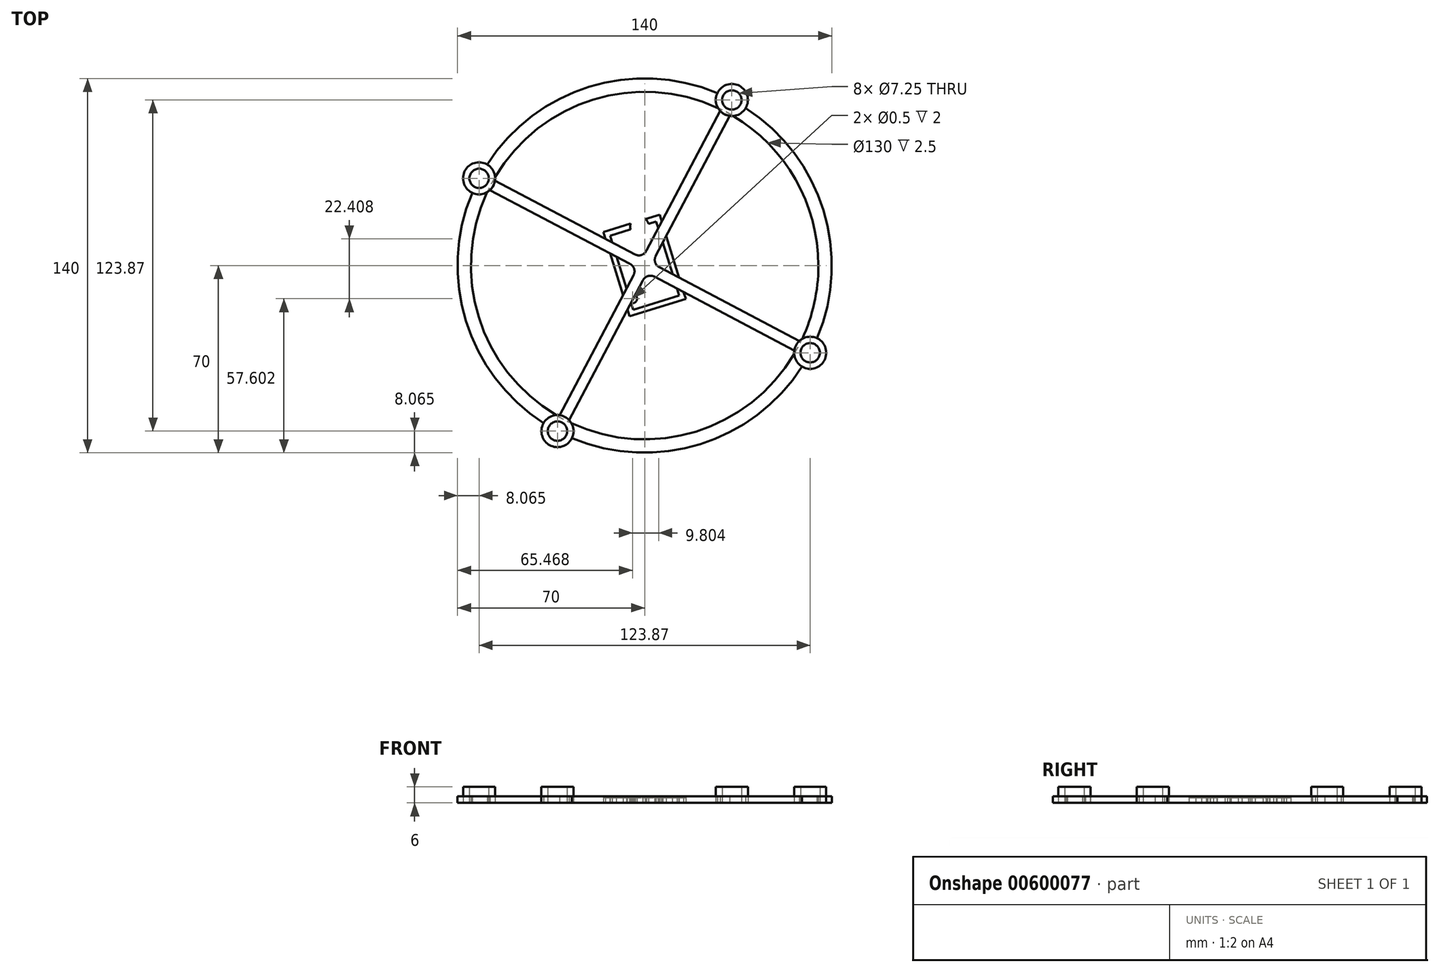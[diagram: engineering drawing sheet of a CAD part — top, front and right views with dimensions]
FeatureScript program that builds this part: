
annotation { "Feature Type Name" : "Feature", "Feature Type Description" : "" }
export const myFeature = defineFeature(function(context is Context, id is Id, definition is map)
    precondition{}
    {
        {
            var Q0;
            Q0=qCreatedBy(makeId("Top.planeOp"),FACE);
            var sketch = newSketch(context, id + "F0", { "sketchPlane" : qUnion([Q0])});
            skCircle(sketch, "E0", {"center": v(-61.93, 32.62) * mm, "radius": 3.62 * mm});
            skCircle(sketch, "E1", {"center": v(-61.93, 32.62) * mm, "radius": 6 * mm});
            skCircle(sketch, "E2", {"center": v(0, 0) * mm, "radius": 70 * mm});
            skCircle(sketch, "E3", {"center": v(0, 0) * mm, "radius": 65 * mm});
            skCircle(sketch, "E4.1.0", {"center": v(-32.62, -61.93) * mm, "radius": 3.62 * mm});
            skCircle(sketch, "E4.1.1", {"center": v(-32.62, -61.93) * mm, "radius": 6 * mm});
            skCircle(sketch, "E4.2.0", {"center": v(61.93, -32.62) * mm, "radius": 3.62 * mm});
            skCircle(sketch, "E4.2.1", {"center": v(61.93, -32.62) * mm, "radius": 6 * mm});
            skCircle(sketch, "E4.3.0", {"center": v(32.62, 61.93) * mm, "radius": 3.62 * mm});
            skCircle(sketch, "E4.3.1", {"center": v(32.62, 61.93) * mm, "radius": 6 * mm});
            skLineSegment(sketch, "E5", {"start": v(32.62, 61.93) * mm, "end": v(-32.62, -61.93) * mm});
            skLineSegment(sketch, "E6", {"start": v(-56.55, 32.05) * mm, "end": v(-3.59, 4.15) * mm});
            skArc(sketch, "E7", {"start": v(-3.59, 4.15) * mm, "mid": v(-1.1, 3.97) * mm, "end": v(0.72, 5.66) * mm});
            skLineSegment(sketch, "E8", {"start": v(0.72, 5.66) * mm, "end": v(28.5, 58.42) * mm});
            skLineSegment(sketch, "E9", {"start": v(61.93, -32.62) * mm, "end": v(-61.93, 32.62) * mm});
            skLineSegment(sketch, "E10.1.0", {"start": v(-5.66, 0.72) * mm, "end": v(-58.42, 28.5) * mm});
            skArc(sketch, "E10.1.1", {"start": v(-4.15, -3.59) * mm, "mid": v(-3.97, -1.1) * mm, "end": v(-5.66, 0.72) * mm});
            skLineSegment(sketch, "E10.1.2", {"start": v(-32.05, -56.55) * mm, "end": v(-4.15, -3.59) * mm});
            skLineSegment(sketch, "E10.2.0", {"start": v(-0.72, -5.66) * mm, "end": v(-28.5, -58.42) * mm});
            skArc(sketch, "E10.2.1", {"start": v(3.59, -4.15) * mm, "mid": v(1.1, -3.97) * mm, "end": v(-0.72, -5.66) * mm});
            skLineSegment(sketch, "E10.2.2", {"start": v(56.55, -32.05) * mm, "end": v(3.59, -4.15) * mm});
            skLineSegment(sketch, "E10.3.0", {"start": v(5.66, -0.72) * mm, "end": v(58.42, -28.5) * mm});
            skArc(sketch, "E10.3.1", {"start": v(4.15, 3.59) * mm, "mid": v(3.97, 1.1) * mm, "end": v(5.66, -0.72) * mm});
            skLineSegment(sketch, "E10.3.2", {"start": v(32.05, 56.55) * mm, "end": v(4.15, 3.59) * mm});
            skSolve(sketch);
        }
        {
            var Q0;
            {var subQ0=sQuery(id+"F0.wireOp",EDGE,"E2");var subQ1=sQuery(id+"F0.wireOp",EDGE,"E0");var subQ2=makeQuery(id+"F0.imprint","INTERSECT",VERTEX,{"disambiguationData":[OD(0.0)],"derivedFrom":[subQ1,subQ0]});Q0=makeQuery(id+"F0.imprint","IMPRINT",FACE,{"disambiguationData":[TD([[makeQuery(id+"F0.imprint","IMPRINT",EDGE,{"disambiguationData":[TD([[subQ2,1.0]])],"derivedFrom":subQ1}),-1.0]])]});}
            var Q1;
            {var subQ3=sQuery(id+"F0.wireOp",EDGE,"E0");var subQ8=sQuery(id+"F0.wireOp",EDGE,"E2");var subQ9=makeQuery(id+"F0.imprint","INTERSECT",VERTEX,{"disambiguationData":[OD(0.0)],"derivedFrom":[subQ3,subQ8]});Q1=makeQuery(id+"F0.imprint","IMPRINT",FACE,{"disambiguationData":[TD([[makeQuery(id+"F0.imprint","IMPRINT",EDGE,{"disambiguationData":[TD([[subQ9,-1.0]])],"derivedFrom":subQ3}),-1.0]])]});}
            var Q2;
            {var subQ3=sQuery(id+"F0.wireOp",EDGE,"E0");var subQ8=sQuery(id+"F0.wireOp",EDGE,"E2");var subQ9=makeQuery(id+"F0.imprint","INTERSECT",VERTEX,{"disambiguationData":[OD(1.0)],"derivedFrom":[subQ3,subQ8]});Q2=makeQuery(id+"F0.imprint","IMPRINT",FACE,{"disambiguationData":[TD([[makeQuery(id+"F0.imprint","IMPRINT",EDGE,{"disambiguationData":[TD([[subQ9,1.0]])],"derivedFrom":subQ3}),-1.0]])]});}
            var Q3;
            {var subQ0=sQuery(id+"F0.wireOp",EDGE,"E9");var subQ3=sQuery(id+"F0.wireOp",EDGE,"E1");var subQ4=makeQuery(id+"F0.imprint","INTERSECT",VERTEX,{"derivedFrom":[subQ3,subQ0]});Q3=makeQuery(id+"F0.imprint","IMPRINT",FACE,{"disambiguationData":[TD([[makeQuery(id+"F0.imprint","IMPRINT",EDGE,{"disambiguationData":[TD([[subQ4,-1.0]])],"derivedFrom":subQ3}),1.0]])]});}
            var Q4;
            {var subQ0=sQuery(id+"F0.wireOp",EDGE,"E10.1.0");var subQ1=sQuery(id+"F0.wireOp",EDGE,"E1");var subQ2=makeQuery(id+"F0.imprint","INTERSECT",VERTEX,{"derivedFrom":[subQ1,subQ0]});Q4=makeQuery(id+"F0.imprint","IMPRINT",FACE,{"disambiguationData":[TD([[makeQuery(id+"F0.imprint","IMPRINT",EDGE,{"disambiguationData":[TD([[subQ2,-1.0]])],"derivedFrom":subQ1}),1.0]])]});}
            var Q5;
            {var subQ1=sQuery(id+"F0.wireOp",EDGE,"E1");var subQ3=sQuery(id+"F0.wireOp",EDGE,"E3");var subQ5=makeQuery(id+"F0.imprint","INTERSECT",VERTEX,{"disambiguationData":[OD(0.0)],"derivedFrom":[subQ1,subQ3]});Q5=makeQuery(id+"F0.imprint","IMPRINT",FACE,{"disambiguationData":[TD([[makeQuery(id+"F0.imprint","IMPRINT",EDGE,{"disambiguationData":[TD([[subQ5,1.0]])],"derivedFrom":subQ1}),1.0]])]});}
            var Q6;
            {var subQ1=sQuery(id+"F0.wireOp",EDGE,"E1");var subQ3=sQuery(id+"F0.wireOp",EDGE,"E3");var subQ5=makeQuery(id+"F0.imprint","INTERSECT",VERTEX,{"disambiguationData":[OD(1.0)],"derivedFrom":[subQ1,subQ3]});Q6=makeQuery(id+"F0.imprint","IMPRINT",FACE,{"disambiguationData":[TD([[makeQuery(id+"F0.imprint","IMPRINT",EDGE,{"disambiguationData":[TD([[subQ5,-1.0]])],"derivedFrom":subQ1}),1.0]])]});}
            var Q7;
            {var subQ0=sQuery(id+"F0.wireOp",EDGE,"E4.3.1");var subQ1=sQuery(id+"F0.wireOp",EDGE,"E2");var subQ3=makeQuery(id+"F0.imprint","INTERSECT",VERTEX,{"disambiguationData":[OD(0.0)],"derivedFrom":[subQ1,subQ0]});Q7=makeQuery(id+"F0.imprint","IMPRINT",FACE,{"disambiguationData":[TD([[makeQuery(id+"F0.imprint","IMPRINT",EDGE,{"disambiguationData":[TD([[subQ3,-1.0]])],"derivedFrom":subQ1}),-1.0]])]});}
            var Q8;
            {var subQ5=sQuery(id+"F0.wireOp",EDGE,"E4.3.1");var subQ7=sQuery(id+"F0.wireOp",EDGE,"E2");var subQ8=makeQuery(id+"F0.imprint","INTERSECT",VERTEX,{"disambiguationData":[OD(0.0)],"derivedFrom":[subQ7,subQ5]});Q8=makeQuery(id+"F0.imprint","IMPRINT",FACE,{"disambiguationData":[TD([[makeQuery(id+"F0.imprint","IMPRINT",EDGE,{"disambiguationData":[TD([[subQ8,-1.0]])],"derivedFrom":subQ7}),1.0]])]});}
            var Q9;
            {var subQ0=sQuery(id+"F0.wireOp",EDGE,"E10.3.2");var subQ3=sQuery(id+"F0.wireOp",EDGE,"E3");var subQ4=makeQuery(id+"F0.imprint","INTERSECT",VERTEX,{"derivedFrom":[subQ3,subQ0]});Q9=makeQuery(id+"F0.imprint","IMPRINT",FACE,{"disambiguationData":[TD([[makeQuery(id+"F0.imprint","IMPRINT",EDGE,{"disambiguationData":[TD([[subQ4,-1.0]])],"derivedFrom":subQ3}),1.0]])]});}
            var Q10;
            {var subQ5=sQuery(id+"F0.wireOp",EDGE,"E4.3.1");var subQ7=sQuery(id+"F0.wireOp",EDGE,"E2");var subQ8=makeQuery(id+"F0.imprint","INTERSECT",VERTEX,{"disambiguationData":[OD(1.0)],"derivedFrom":[subQ7,subQ5]});Q10=makeQuery(id+"F0.imprint","IMPRINT",FACE,{"disambiguationData":[TD([[makeQuery(id+"F0.imprint","IMPRINT",EDGE,{"disambiguationData":[TD([[subQ8,1.0]])],"derivedFrom":subQ7}),1.0]])]});}
            var Q11;
            {var subQ0=sQuery(id+"F0.wireOp",EDGE,"E10.3.2");var subQ3=sQuery(id+"F0.wireOp",EDGE,"E3");var subQ4=makeQuery(id+"F0.imprint","INTERSECT",VERTEX,{"derivedFrom":[subQ3,subQ0]});Q11=makeQuery(id+"F0.imprint","IMPRINT",FACE,{"disambiguationData":[TD([[makeQuery(id+"F0.imprint","IMPRINT",EDGE,{"disambiguationData":[TD([[subQ4,1.0]])],"derivedFrom":subQ3}),1.0]])]});}
            var Q12;
            {var subQ0=sQuery(id+"F0.wireOp",EDGE,"E8");var subQ3=sQuery(id+"F0.wireOp",EDGE,"E3");var subQ4=makeQuery(id+"F0.imprint","INTERSECT",VERTEX,{"derivedFrom":[subQ3,subQ0]});Q12=makeQuery(id+"F0.imprint","IMPRINT",FACE,{"disambiguationData":[TD([[makeQuery(id+"F0.imprint","IMPRINT",EDGE,{"disambiguationData":[TD([[subQ4,1.0]])],"derivedFrom":subQ3}),1.0]])]});}
            var Q13;
            {var subQ0=sQuery(id+"F0.wireOp",EDGE,"E8");var subQ3=sQuery(id+"F0.wireOp",EDGE,"E3");var subQ4=makeQuery(id+"F0.imprint","INTERSECT",VERTEX,{"derivedFrom":[subQ3,subQ0]});Q13=makeQuery(id+"F0.imprint","IMPRINT",FACE,{"disambiguationData":[TD([[makeQuery(id+"F0.imprint","IMPRINT",EDGE,{"disambiguationData":[TD([[subQ4,-1.0]])],"derivedFrom":subQ3}),1.0]])]});}
            var Q14;
            {var subQ0=sQuery(id+"F0.wireOp",EDGE,"E4.2.1");var subQ1=sQuery(id+"F0.wireOp",EDGE,"E2");var subQ3=makeQuery(id+"F0.imprint","INTERSECT",VERTEX,{"disambiguationData":[OD(0.0)],"derivedFrom":[subQ1,subQ0]});Q14=makeQuery(id+"F0.imprint","IMPRINT",FACE,{"disambiguationData":[TD([[makeQuery(id+"F0.imprint","IMPRINT",EDGE,{"disambiguationData":[TD([[subQ3,-1.0]])],"derivedFrom":subQ1}),-1.0]])]});}
            var Q15;
            {var subQ5=sQuery(id+"F0.wireOp",EDGE,"E2");var subQ7=sQuery(id+"F0.wireOp",EDGE,"E4.2.1");var subQ10=makeQuery(id+"F0.imprint","INTERSECT",VERTEX,{"disambiguationData":[OD(1.0)],"derivedFrom":[subQ5,subQ7]});Q15=makeQuery(id+"F0.imprint","IMPRINT",FACE,{"disambiguationData":[TD([[makeQuery(id+"F0.imprint","IMPRINT",EDGE,{"disambiguationData":[TD([[subQ10,1.0]])],"derivedFrom":subQ5}),1.0]])]});}
            var Q16;
            {var subQ0=sQuery(id+"F0.wireOp",EDGE,"E10.3.0");var subQ3=sQuery(id+"F0.wireOp",EDGE,"E3");var subQ4=makeQuery(id+"F0.imprint","INTERSECT",VERTEX,{"derivedFrom":[subQ3,subQ0]});Q16=makeQuery(id+"F0.imprint","IMPRINT",FACE,{"disambiguationData":[TD([[makeQuery(id+"F0.imprint","IMPRINT",EDGE,{"disambiguationData":[TD([[subQ4,-1.0]])],"derivedFrom":subQ3}),1.0]])]});}
            var Q17;
            {var subQ0=sQuery(id+"F0.wireOp",EDGE,"E10.3.0");var subQ3=sQuery(id+"F0.wireOp",EDGE,"E3");var subQ4=makeQuery(id+"F0.imprint","INTERSECT",VERTEX,{"derivedFrom":[subQ3,subQ0]});Q17=makeQuery(id+"F0.imprint","IMPRINT",FACE,{"disambiguationData":[TD([[makeQuery(id+"F0.imprint","IMPRINT",EDGE,{"disambiguationData":[TD([[subQ4,1.0]])],"derivedFrom":subQ3}),1.0]])]});}
            var Q18;
            {var subQ0=sQuery(id+"F0.wireOp",EDGE,"E10.2.2");var subQ3=sQuery(id+"F0.wireOp",EDGE,"E3");var subQ4=makeQuery(id+"F0.imprint","INTERSECT",VERTEX,{"derivedFrom":[subQ3,subQ0]});Q18=makeQuery(id+"F0.imprint","IMPRINT",FACE,{"disambiguationData":[TD([[makeQuery(id+"F0.imprint","IMPRINT",EDGE,{"disambiguationData":[TD([[subQ4,-1.0]])],"derivedFrom":subQ3}),1.0]])]});}
            var Q19;
            {var subQ5=sQuery(id+"F0.wireOp",EDGE,"E4.2.1");var subQ7=sQuery(id+"F0.wireOp",EDGE,"E2");var subQ8=makeQuery(id+"F0.imprint","INTERSECT",VERTEX,{"disambiguationData":[OD(0.0)],"derivedFrom":[subQ7,subQ5]});Q19=makeQuery(id+"F0.imprint","IMPRINT",FACE,{"disambiguationData":[TD([[makeQuery(id+"F0.imprint","IMPRINT",EDGE,{"disambiguationData":[TD([[subQ8,-1.0]])],"derivedFrom":subQ7}),1.0]])]});}
            var Q20;
            {var subQ0=sQuery(id+"F0.wireOp",EDGE,"E10.2.2");var subQ3=sQuery(id+"F0.wireOp",EDGE,"E3");var subQ4=makeQuery(id+"F0.imprint","INTERSECT",VERTEX,{"derivedFrom":[subQ3,subQ0]});Q20=makeQuery(id+"F0.imprint","IMPRINT",FACE,{"disambiguationData":[TD([[makeQuery(id+"F0.imprint","IMPRINT",EDGE,{"disambiguationData":[TD([[subQ4,1.0]])],"derivedFrom":subQ3}),1.0]])]});}
            var Q21;
            {var subQ5=sQuery(id+"F0.wireOp",EDGE,"E4.1.1");var subQ7=sQuery(id+"F0.wireOp",EDGE,"E2");var subQ8=makeQuery(id+"F0.imprint","INTERSECT",VERTEX,{"disambiguationData":[OD(1.0)],"derivedFrom":[subQ7,subQ5]});Q21=makeQuery(id+"F0.imprint","IMPRINT",FACE,{"disambiguationData":[TD([[makeQuery(id+"F0.imprint","IMPRINT",EDGE,{"disambiguationData":[TD([[subQ8,1.0]])],"derivedFrom":subQ7}),1.0]])]});}
            var Q22;
            {var subQ0=sQuery(id+"F0.wireOp",EDGE,"E10.2.0");var subQ3=sQuery(id+"F0.wireOp",EDGE,"E3");var subQ4=makeQuery(id+"F0.imprint","INTERSECT",VERTEX,{"derivedFrom":[subQ3,subQ0]});Q22=makeQuery(id+"F0.imprint","IMPRINT",FACE,{"disambiguationData":[TD([[makeQuery(id+"F0.imprint","IMPRINT",EDGE,{"disambiguationData":[TD([[subQ4,1.0]])],"derivedFrom":subQ3}),1.0]])]});}
            var Q23;
            {var subQ0=sQuery(id+"F0.wireOp",EDGE,"E10.2.0");var subQ3=sQuery(id+"F0.wireOp",EDGE,"E3");var subQ4=makeQuery(id+"F0.imprint","INTERSECT",VERTEX,{"derivedFrom":[subQ3,subQ0]});Q23=makeQuery(id+"F0.imprint","IMPRINT",FACE,{"disambiguationData":[TD([[makeQuery(id+"F0.imprint","IMPRINT",EDGE,{"disambiguationData":[TD([[subQ4,-1.0]])],"derivedFrom":subQ3}),1.0]])]});}
            var Q24;
            {var subQ0=sQuery(id+"F0.wireOp",EDGE,"E10.1.2");var subQ3=sQuery(id+"F0.wireOp",EDGE,"E3");var subQ4=makeQuery(id+"F0.imprint","INTERSECT",VERTEX,{"derivedFrom":[subQ3,subQ0]});Q24=makeQuery(id+"F0.imprint","IMPRINT",FACE,{"disambiguationData":[TD([[makeQuery(id+"F0.imprint","IMPRINT",EDGE,{"disambiguationData":[TD([[subQ4,-1.0]])],"derivedFrom":subQ3}),1.0]])]});}
            var Q25;
            {var subQ0=sQuery(id+"F0.wireOp",EDGE,"E10.1.2");var subQ3=sQuery(id+"F0.wireOp",EDGE,"E3");var subQ4=makeQuery(id+"F0.imprint","INTERSECT",VERTEX,{"derivedFrom":[subQ3,subQ0]});Q25=makeQuery(id+"F0.imprint","IMPRINT",FACE,{"disambiguationData":[TD([[makeQuery(id+"F0.imprint","IMPRINT",EDGE,{"disambiguationData":[TD([[subQ4,1.0]])],"derivedFrom":subQ3}),1.0]])]});}
            var Q26;
            {var subQ0=sQuery(id+"F0.wireOp",EDGE,"E4.1.1");var subQ3=sQuery(id+"F0.wireOp",EDGE,"E2");var subQ4=makeQuery(id+"F0.imprint","INTERSECT",VERTEX,{"disambiguationData":[OD(0.0)],"derivedFrom":[subQ3,subQ0]});Q26=makeQuery(id+"F0.imprint","IMPRINT",FACE,{"disambiguationData":[TD([[makeQuery(id+"F0.imprint","IMPRINT",EDGE,{"disambiguationData":[TD([[subQ4,-1.0]])],"derivedFrom":subQ3}),1.0]])]});}
            var Q27;
            {var subQ1=sQuery(id+"F0.wireOp",EDGE,"E2");var subQ4=sQuery(id+"F0.wireOp",EDGE,"E4.1.1");var subQ6=makeQuery(id+"F0.imprint","INTERSECT",VERTEX,{"disambiguationData":[OD(0.0)],"derivedFrom":[subQ1,subQ4]});Q27=makeQuery(id+"F0.imprint","IMPRINT",FACE,{"disambiguationData":[TD([[makeQuery(id+"F0.imprint","IMPRINT",EDGE,{"disambiguationData":[TD([[subQ6,-1.0]])],"derivedFrom":subQ1}),-1.0]])]});}
            extrude(context, id + "F1", {"entities" : qUnion([Q0, Q1, Q2, Q3, Q4, Q5, Q6, Q7, Q8, Q9, Q10, Q11, Q12, Q13, Q14, Q15, Q16, Q17, Q18, Q19, Q20, Q21, Q22, Q23, Q24, Q25, Q26, Q27]), "depth" : 6 * mm});
        }
        {
            var Q0;
            Q0=qSketchRegion(id+"F0",true);
            var Q1;
            {var subQ3=sQuery(id+"F0.wireOp",EDGE,"E10.3.1");Q1=makeQuery(id+"F0.imprint","IMPRINT",FACE,{"disambiguationData":[TD([[makeQuery(id+"F0.imprint","IMPRINT",EDGE,{"derivedFrom":subQ3}),-1.0]])]});}
            var Q2;
            {var subQ3=sQuery(id+"F0.wireOp",EDGE,"E7");Q2=makeQuery(id+"F0.imprint","IMPRINT",FACE,{"disambiguationData":[TD([[makeQuery(id+"F0.imprint","IMPRINT",EDGE,{"derivedFrom":subQ3}),-1.0]])]});}
            var Q3;
            {var subQ3=sQuery(id+"F0.wireOp",EDGE,"E10.1.1");Q3=makeQuery(id+"F0.imprint","IMPRINT",FACE,{"disambiguationData":[TD([[makeQuery(id+"F0.imprint","IMPRINT",EDGE,{"derivedFrom":subQ3}),-1.0]])]});}
            var Q4;
            {var subQ3=sQuery(id+"F0.wireOp",EDGE,"E10.2.1");Q4=makeQuery(id+"F0.imprint","IMPRINT",FACE,{"disambiguationData":[TD([[makeQuery(id+"F0.imprint","IMPRINT",EDGE,{"derivedFrom":subQ3}),-1.0]])]});}
            extrude(context, id + "F2", {"entities" : qUnion([Q0, Q1, Q2, Q3, Q4]), "depth" : 2.5 * mm});
        }
        {
            var Q0;
            {var subQ3=sQuery(id+"F0.wireOp",EDGE,"E10.3.1");Q0=makeQuery(id+"F0.imprint","IMPRINT",FACE,{"disambiguationData":[TD([[makeQuery(id+"F0.imprint","IMPRINT",EDGE,{"derivedFrom":subQ3}),-1.0]])]});}
            var sketch = newSketch(context, id + "F3", { "sketchPlane" : qUnion([Q0])});
            skLineSegment(sketch, "E11", {"start": v(-32.62, -61.93) * mm, "end": v(-61.93, 32.62) * mm, "construction": true});
            skLineSegment(sketch, "E12", {"start": v(-61.93, 32.62) * mm, "end": v(32.62, 61.93) * mm, "construction": true});
            skLineSegment(sketch, "E13", {"start": v(32.62, 61.93) * mm, "end": v(61.93, -32.62) * mm, "construction": true});
            skLineSegment(sketch, "E14", {"start": v(61.93, -32.62) * mm, "end": v(-32.62, -61.93) * mm, "construction": true});
            skLineSegment(sketch, "E15", {"start": v(-4.3, -16.51) * mm, "end": v(12.9, -11.18) * mm});
            skLineSegment(sketch, "E16", {"start": v(12.9, -11.18) * mm, "end": v(4.3, 16.51) * mm});
            skLineSegment(sketch, "E17", {"start": v(4.3, 16.51) * mm, "end": v(-12.9, 11.18) * mm});
            skLineSegment(sketch, "E18", {"start": v(-12.9, 11.18) * mm, "end": v(-4.3, -16.51) * mm});
            skLineSegment(sketch, "E19.0", {"start": v(-15.4, 12.5) * mm, "end": v(-5.62, -19.02) * mm});
            skLineSegment(sketch, "E19.1", {"start": v(5.62, 19.02) * mm, "end": v(-15.4, 12.5) * mm});
            skLineSegment(sketch, "E19.2", {"start": v(15.4, -12.5) * mm, "end": v(5.62, 19.02) * mm});
            skLineSegment(sketch, "E19.3", {"start": v(-5.62, -19.02) * mm, "end": v(15.4, -12.5) * mm});
            skCircle(sketch, "E20", {"center": v(-1.9, 14.59) * mm, "radius": 3.5 * mm});
            skCircle(sketch, "E21", {"center": v(-1.9, 14.59) * mm, "radius": 5.5 * mm});
            skCircle(sketch, "E22", {"center": v(-4.53, -12.4) * mm, "radius": 1.7 * mm});
            skCircle(sketch, "E23", {"center": v(-4.53, -12.4) * mm, "radius": 0.25 * mm});
            skLineSegment(sketch, "E24", {"start": v(-4.03, -14.02) * mm, "end": v(-4.98, -14.32) * mm});
            skLineSegment(sketch, "E25", {"start": v(-5.04, -10.77) * mm, "end": v(-6, -11.07) * mm});
            skCircle(sketch, "E26", {"center": v(5.27, 10.01) * mm, "radius": 1.7 * mm});
            skCircle(sketch, "E27", {"center": v(5.27, 10.01) * mm, "radius": 0.25 * mm});
            skLineSegment(sketch, "E28", {"start": v(5.78, 8.39) * mm, "end": v(6.73, 8.68) * mm});
            skLineSegment(sketch, "E29", {"start": v(4.77, 11.63) * mm, "end": v(5.72, 11.93) * mm});
            skSolve(sketch);
        }
        {
            var Q0;
            Q0=makeQuery(id+"F3.imprint","IMPRINT",FACE,{"disambiguationData":[TD([[makeQuery(id+"F3.imprint","IMPRINT",EDGE,{"derivedFrom":sQuery(id+"F3.wireOp",EDGE,"E23")}),1.0]])]});
            var Q1;
            {var subQ0=sQuery(id+"F0.wireOp",EDGE,"E5");var subQ1=makeQuery(id+"F0.imprint","IMPRINT",EDGE,{"disambiguationData":[TD([[makeQuery(id+"F0.imprint","INTERSECT",VERTEX,{"derivedFrom":[sQuery(id+"F0.wireOp",EDGE,"E4.3.1"),subQ0]}),-1.0]])],"derivedFrom":subQ0});var subQ2=sQuery(id+"F3.wireOp",EDGE,"E27");var subQ4=makeQuery(id+"F3.imprint","INTERSECT",VERTEX,{"disambiguationData":[OD(0.0)],"derivedFrom":[subQ1,subQ2]});Q1=makeQuery(id+"F3.imprint","IMPRINT",FACE,{"disambiguationData":[TD([[makeQuery(id+"F3.imprint","IMPRINT",EDGE,{"disambiguationData":[TD([[subQ4,-1.0]])],"derivedFrom":subQ2}),1.0]])]});}
            var Q2;
            {var subQ0=sQuery(id+"F0.wireOp",EDGE,"E5");var subQ1=makeQuery(id+"F0.imprint","IMPRINT",EDGE,{"disambiguationData":[TD([[makeQuery(id+"F0.imprint","INTERSECT",VERTEX,{"derivedFrom":[sQuery(id+"F0.wireOp",EDGE,"E4.3.1"),subQ0]}),-1.0]])],"derivedFrom":subQ0});var subQ2=sQuery(id+"F3.wireOp",EDGE,"E27");var subQ4=makeQuery(id+"F3.imprint","INTERSECT",VERTEX,{"disambiguationData":[OD(0.0)],"derivedFrom":[subQ1,subQ2]});Q2=makeQuery(id+"F3.imprint","IMPRINT",FACE,{"disambiguationData":[TD([[makeQuery(id+"F3.imprint","IMPRINT",EDGE,{"disambiguationData":[TD([[subQ4,1.0]])],"derivedFrom":subQ2}),1.0]])]});}
            extrude(context, id + "F4", {"entities" : qUnion([Q0, Q1, Q2]), "operationType" : NewBodyOperationType.REMOVE, "depth" : 2 * mm});
        }
        {
            var Q0;
            {var subQ18=sQuery(id+"F3.wireOp",EDGE,"E15");Q0=makeQuery(id+"F3.imprint","IMPRINT",FACE,{"disambiguationData":[TD([[makeQuery(id+"F3.imprint","IMPRINT",EDGE,{"derivedFrom":subQ18}),-1.0]])]});}
            var Q1;
            {var subQ1=sQuery(id+"F3.wireOp",EDGE,"E17");var subQ5=sQuery(id+"F3.wireOp",EDGE,"E20");var subQ7=makeQuery(id+"F3.imprint","INTERSECT",VERTEX,{"disambiguationData":[OD(1.0)],"derivedFrom":[subQ1,subQ5]});Q1=makeQuery(id+"F3.imprint","IMPRINT",FACE,{"disambiguationData":[TD([[makeQuery(id+"F3.imprint","IMPRINT",EDGE,{"disambiguationData":[TD([[subQ7,-1.0]])],"derivedFrom":subQ1}),-1.0]])]});}
            var Q2;
            {var subQ0=sQuery(id+"F3.wireOp",EDGE,"E21");var subQ1=sQuery(id+"F3.wireOp",EDGE,"E19.1");var subQ3=makeQuery(id+"F3.imprint","INTERSECT",VERTEX,{"disambiguationData":[OD(0.0)],"derivedFrom":[subQ1,subQ0]});Q2=makeQuery(id+"F3.imprint","IMPRINT",FACE,{"disambiguationData":[TD([[makeQuery(id+"F3.imprint","IMPRINT",EDGE,{"disambiguationData":[TD([[subQ3,-1.0]])],"derivedFrom":subQ1}),-1.0]])]});}
            var Q3;
            {var subQ0=sQuery(id+"F3.wireOp",EDGE,"E21");var subQ1=sQuery(id+"F3.wireOp",EDGE,"E17");var subQ2=makeQuery(id+"F3.imprint","INTERSECT",VERTEX,{"disambiguationData":[OD(0.0)],"derivedFrom":[subQ1,subQ0]});Q3=makeQuery(id+"F3.imprint","IMPRINT",FACE,{"disambiguationData":[TD([[makeQuery(id+"F3.imprint","IMPRINT",EDGE,{"disambiguationData":[TD([[subQ2,-1.0]])],"derivedFrom":subQ1}),-1.0]])]});}
            var Q4;
            {var subQ12=sQuery(id+"F3.wireOp",EDGE,"E16");var subQ15=makeQuery(id+"F3.imprint","INTERSECT",VERTEX,{"derivedFrom":[subQ12,sQuery(id+"F3.wireOp",EDGE,"E29")]});Q4=makeQuery(id+"F3.imprint","IMPRINT",FACE,{"disambiguationData":[TD([[makeQuery(id+"F3.imprint","IMPRINT",EDGE,{"disambiguationData":[TD([[subQ15,1.0]])],"derivedFrom":subQ12}),-1.0]])]});}
            var Q5;
            {var subQ0=sQuery(id+"F0.wireOp",EDGE,"E10.3.0");var subQ1=sQuery(id+"F0.wireOp",EDGE,"E10.3.1");var subQ2=makeQuery(id+"F0.imprint","IMPRINT",EDGE,{"disambiguationData":[TD([[makeQuery(id+"F0.imprint","INTERSECT",VERTEX,{"derivedFrom":[subQ0,subQ1]}),-1.0]])],"derivedFrom":subQ0});var subQ3=sQuery(id+"F3.wireOp",EDGE,"E16");var subQ4=makeQuery(id+"F3.imprint","INTERSECT",VERTEX,{"derivedFrom":[subQ2,subQ3]});Q5=makeQuery(id+"F3.imprint","IMPRINT",FACE,{"disambiguationData":[TD([[makeQuery(id+"F3.imprint","IMPRINT",EDGE,{"disambiguationData":[TD([[subQ4,-1.0]])],"derivedFrom":subQ3}),-1.0]])]});}
            var Q6;
            {var subQ0=sQuery(id+"F0.wireOp",EDGE,"E9");var subQ1=sQuery(id+"F0.wireOp",EDGE,"E4.2.1");var subQ2=makeQuery(id+"F0.imprint","IMPRINT",EDGE,{"disambiguationData":[TD([[makeQuery(id+"F0.imprint","INTERSECT",VERTEX,{"derivedFrom":[subQ1,subQ0]}),-1.0]])],"derivedFrom":subQ0});var subQ3=sQuery(id+"F3.wireOp",EDGE,"E16");var subQ4=makeQuery(id+"F3.imprint","INTERSECT",VERTEX,{"derivedFrom":[subQ2,subQ3]});Q6=makeQuery(id+"F3.imprint","IMPRINT",FACE,{"disambiguationData":[TD([[makeQuery(id+"F3.imprint","IMPRINT",EDGE,{"disambiguationData":[TD([[subQ4,-1.0]])],"derivedFrom":subQ3}),-1.0]])]});}
            var Q7;
            {var subQ9=sQuery(id+"F3.wireOp",EDGE,"E16");var subQ13=makeQuery(id+"F3.imprint","INTERSECT",VERTEX,{"derivedFrom":[subQ9,sQuery(id+"F3.wireOp",EDGE,"E28")]});Q7=makeQuery(id+"F3.imprint","IMPRINT",FACE,{"disambiguationData":[TD([[makeQuery(id+"F3.imprint","IMPRINT",EDGE,{"disambiguationData":[TD([[subQ13,-1.0]])],"derivedFrom":subQ9}),-1.0]])]});}
            var Q8;
            {var subQ2=sQuery(id+"F3.wireOp",EDGE,"E26");var subQ4=sQuery(id+"F3.wireOp",EDGE,"E16");var subQ6=makeQuery(id+"F3.imprint","INTERSECT",VERTEX,{"disambiguationData":[OD(0.0)],"derivedFrom":[subQ4,subQ2]});Q8=makeQuery(id+"F3.imprint","IMPRINT",FACE,{"disambiguationData":[TD([[makeQuery(id+"F3.imprint","IMPRINT",EDGE,{"disambiguationData":[TD([[subQ6,-1.0]])],"derivedFrom":subQ4}),-1.0]])]});}
            var Q9;
            {var subQ7=sQuery(id+"F3.wireOp",EDGE,"E26");var subQ9=makeQuery(id+"F3.imprint","INTERSECT",VERTEX,{"derivedFrom":[subQ7,sQuery(id+"F3.wireOp",EDGE,"E29")]});Q9=makeQuery(id+"F3.imprint","IMPRINT",FACE,{"disambiguationData":[TD([[makeQuery(id+"F3.imprint","IMPRINT",EDGE,{"disambiguationData":[TD([[subQ9,1.0]])],"derivedFrom":subQ7}),1.0]])]});}
            var Q10;
            {var subQ4=sQuery(id+"F3.wireOp",EDGE,"E26");var subQ9=makeQuery(id+"F3.imprint","INTERSECT",VERTEX,{"derivedFrom":[subQ4,sQuery(id+"F3.wireOp",EDGE,"E28")]});Q10=makeQuery(id+"F3.imprint","IMPRINT",FACE,{"disambiguationData":[TD([[makeQuery(id+"F3.imprint","IMPRINT",EDGE,{"disambiguationData":[TD([[subQ9,-1.0]])],"derivedFrom":subQ4}),1.0]])]});}
            var Q11;
            {var subQ0=sQuery(id+"F3.wireOp",EDGE,"E28");Q11=makeQuery(id+"F3.imprint","IMPRINT",FACE,{"disambiguationData":[TD([[makeQuery(id+"F3.imprint","IMPRINT",EDGE,{"derivedFrom":subQ0}),1.0]])]});}
            var Q12;
            {var subQ0=sQuery(id+"F3.wireOp",EDGE,"E25");Q12=makeQuery(id+"F3.imprint","IMPRINT",FACE,{"disambiguationData":[TD([[makeQuery(id+"F3.imprint","IMPRINT",EDGE,{"derivedFrom":subQ0}),1.0]])]});}
            var Q13;
            Q13=makeQuery(id+"F3.imprint","IMPRINT",FACE,{"disambiguationData":[TD([[makeQuery(id+"F3.imprint","IMPRINT",EDGE,{"derivedFrom":sQuery(id+"F3.wireOp",EDGE,"E23")}),-1.0]])]});
            var Q14;
            {var subQ0=sQuery(id+"F3.wireOp",EDGE,"E22");var subQ1=sQuery(id+"F3.wireOp",EDGE,"E18");var subQ3=makeQuery(id+"F3.imprint","INTERSECT",VERTEX,{"disambiguationData":[OD(0.0)],"derivedFrom":[subQ1,subQ0]});Q14=makeQuery(id+"F3.imprint","IMPRINT",FACE,{"disambiguationData":[TD([[makeQuery(id+"F3.imprint","IMPRINT",EDGE,{"disambiguationData":[TD([[subQ3,-1.0]])],"derivedFrom":subQ1}),-1.0]])]});}
            var Q15;
            {var subQ0=sQuery(id+"F3.wireOp",EDGE,"E29");Q15=makeQuery(id+"F3.imprint","IMPRINT",FACE,{"disambiguationData":[TD([[makeQuery(id+"F3.imprint","IMPRINT",EDGE,{"derivedFrom":subQ0}),-1.0]])]});}
            var Q16;
            {var subQ2=sQuery(id+"F3.wireOp",EDGE,"E26");var subQ4=sQuery(id+"F3.wireOp",EDGE,"E16");var subQ6=makeQuery(id+"F3.imprint","INTERSECT",VERTEX,{"disambiguationData":[OD(1.0)],"derivedFrom":[subQ4,subQ2]});Q16=makeQuery(id+"F3.imprint","IMPRINT",FACE,{"disambiguationData":[TD([[makeQuery(id+"F3.imprint","IMPRINT",EDGE,{"disambiguationData":[TD([[subQ6,1.0]])],"derivedFrom":subQ4}),-1.0]])]});}
            var Q17;
            {var subQ0=sQuery(id+"F3.wireOp",EDGE,"E24");Q17=makeQuery(id+"F3.imprint","IMPRINT",FACE,{"disambiguationData":[TD([[makeQuery(id+"F3.imprint","IMPRINT",EDGE,{"derivedFrom":subQ0}),-1.0]])]});}
            extrude(context, id + "F5", {"entities" : qUnion([Q0, Q1, Q2, Q3, Q4, Q5, Q6, Q7, Q8, Q9, Q10, Q11, Q12, Q13, Q14, Q15, Q16, Q17]), "operationType" : NewBodyOperationType.ADD, "depth" : 2 * mm});
        }
    });
